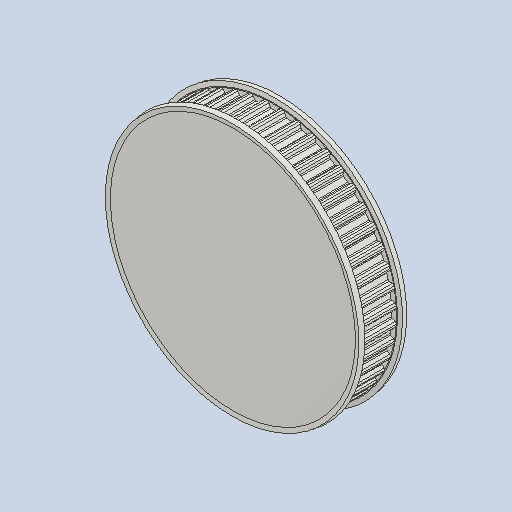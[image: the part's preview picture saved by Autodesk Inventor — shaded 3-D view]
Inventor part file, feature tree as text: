
AUTODESK INVENTOR PART (.ipt)
format: ipt  version: 2025.2 (Build 292293000, 293)  size: 578,048 bytes
history: native  units: mm (DEFAULTED — no unit token found)
features: other x3, extrude x2, fillet x1, pattern_circular x1
ambient origin geometry x8: Origin, YZ Plane, XZ Plane, XY Plane, X Axis, Y Axis, Z Axis, Center Point
bodies: Solid1 (feature_tree)
feature tree (7):
  other  "Pulley Sketch"
  extrude  "Base Body"  Depth=38.197186mm
  extrude  "Tooth"  Depth=0.3mm
  fillet  "Tooth Fillet"  Radius=0.75mm
  pattern_circular  "Teeth"  [2 undecoded]
  other  "Left flange"
  other  "Right flange"
note: 2 required parameter values undecoded (feature->parameter linkage not recoverable at this tier; creation-order binding heuristic only, values carry confidence <= 0.55)
